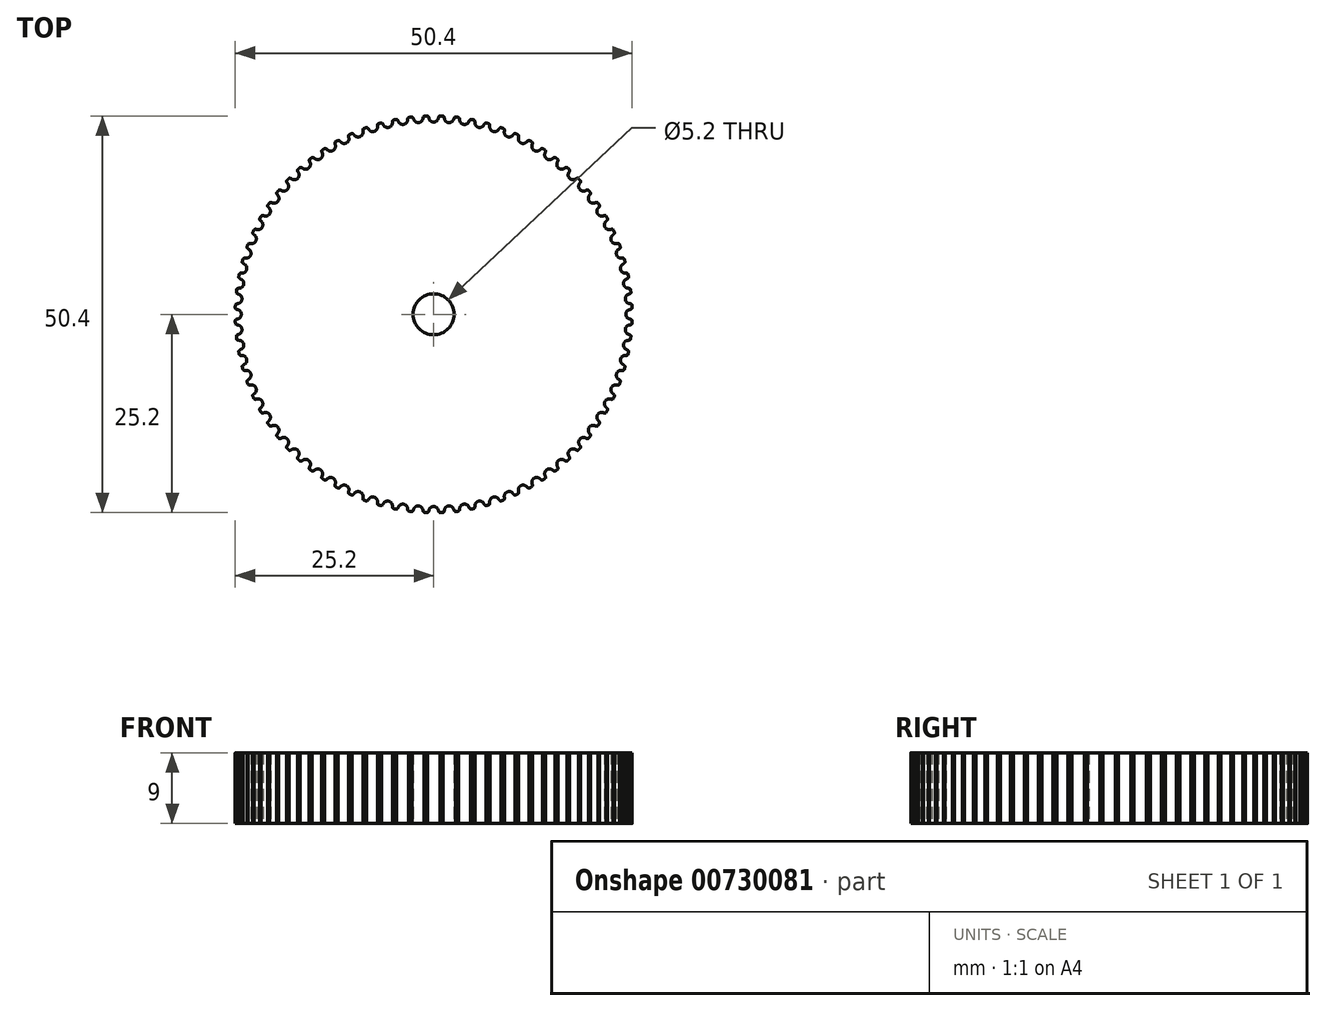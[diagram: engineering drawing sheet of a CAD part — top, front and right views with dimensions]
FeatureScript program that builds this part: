
annotation { "Feature Type Name" : "Feature", "Feature Type Description" : "" }
export const myFeature = defineFeature(function(context is Context, id is Id, definition is map)
    precondition{}
    {
        {
            assignVariable(context, id + "F0", {"name" : "Teeth", "anyValue" : 80});
        }
        {
            var Q0;
            Q0=qCreatedBy(makeId("Top.planeOp"),FACE);
            var sketch = newSketch(context, id + "F1", { "sketchPlane" : qUnion([Q0])});
            skCircle(sketch, "E0", {"center": v(0, 0) * mm, "radius": 25.21 * mm});
            skSolve(sketch);
        }
        {
            var Q0;
            Q0=qCreatedBy(makeId("Top.planeOp"),FACE);
            var sketch = newSketch(context, id + "F2", { "sketchPlane" : qUnion([Q0])});
            skArc(sketch, "E1.0", {"start": v(0.79, 25.2) * mm, "mid": v(0, 25.21) * mm, "end": v(-0.79, 25.2) * mm});
            skLineSegment(sketch, "E2", {"start": v(0, 0) * mm, "end": v(0, 25.03) * mm, "construction": true});
            skArc(sketch, "E3", {"start": v(0, 24.42) * mm, "mid": v(-0.38, 24.56) * mm, "end": v(-0.6, 24.9) * mm});
            skArc(sketch, "E4", {"start": v(-0.6, 24.9) * mm, "mid": v(-0.63, 25) * mm, "end": v(-0.68, 25.1) * mm});
            skArc(sketch, "E5", {"start": v(-0.68, 25.1) * mm, "mid": v(-0.72, 25.16) * mm, "end": v(-0.79, 25.2) * mm});
            skArc(sketch, "E6.MirrorCS", {"start": v(0, 24.42) * mm, "mid": v(0.38, 24.56) * mm, "end": v(0.6, 24.9) * mm});
            skArc(sketch, "E7.MirrorCS", {"start": v(0.68, 25.1) * mm, "mid": v(0.72, 25.16) * mm, "end": v(0.79, 25.2) * mm});
            skArc(sketch, "E8.MirrorCS", {"start": v(0.6, 24.9) * mm, "mid": v(0.63, 25) * mm, "end": v(0.68, 25.1) * mm});
            skSolve(sketch);
        }
        {
            var Q0;
            Q0 = qSketchRegion(id + "F1", true);
            extrude(context, id + "F3", {"entities" : qUnion([Q0]), "depth" : 9 * mm, "offsetDistance" : 25 * mm});
        }
        {
            var Q0;
            Q0=makeQuery(id+"F2.imprint","IMPRINT",FACE,{"disambiguationData":[TD([[makeQuery(id+"F2.imprint","IMPRINT",EDGE,{"derivedFrom":sQuery(id+"F2.wireOp",EDGE,"E1.0")}),1.0]])]});
            extrude(context, id + "F4", {"entities" : qUnion([Q0]), "depth" : 25 * mm, "offsetDistance" : 25 * mm});
        }
        {
            var Q0;
            Q0=makeQuery(id+"F4.opExtrude","SWEPT_BODY",BODY,{"disambiguationData":[OSD([sQuery(id+"F2.wireOp",EDGE,"E1.0"),sQuery(id+"F2.wireOp",EDGE,"E3"),sQuery(id+"F2.wireOp",EDGE,"E4"),sQuery(id+"F2.wireOp",EDGE,"E5"),sQuery(id+"F2.wireOp",EDGE,"E6.MirrorCS"),sQuery(id+"F2.wireOp",EDGE,"E7.MirrorCS"),sQuery(id+"F2.wireOp",EDGE,"E8.MirrorCS")])]});
            var Q1;
            Q1=sQuery(id+"F1.wireOp",EDGE,"E0");
            circularPattern(context, id + "F5", {"operationType" : NewBodyOperationType.REMOVE, "entities" : qUnion([Q0]), "axis" : qUnion([Q1]), "angle" : 360 * degree, "instanceCount" : getVariable(context, 'Teeth'), "equalSpace" : true});
        }
        {
            var Q0;
            Q0=qCreatedBy(makeId("Top.planeOp"),FACE);
            var sketch = newSketch(context, id + "F6", { "sketchPlane" : qUnion([Q0])});
            skCircle(sketch, "E9", {"center": v(0, 0) * mm, "radius": 2.6 * mm});
            skSolve(sketch);
        }
        {
            var Q0;
            Q0 = qSketchRegion(id + "F6", true);
            var Q1;
            Q1=sQuery(id+"F6.wireOp",EDGE,"E9");
            extrude(context, id + "F7", {"entities" : qUnion([Q0]), "operationType" : NewBodyOperationType.REMOVE, "surfaceEntities" : qUnion([Q1]), "endBound" : BoundingType.THROUGH_ALL, "depth" : 25 * mm, "offsetDistance" : 25 * mm});
        }
    });
